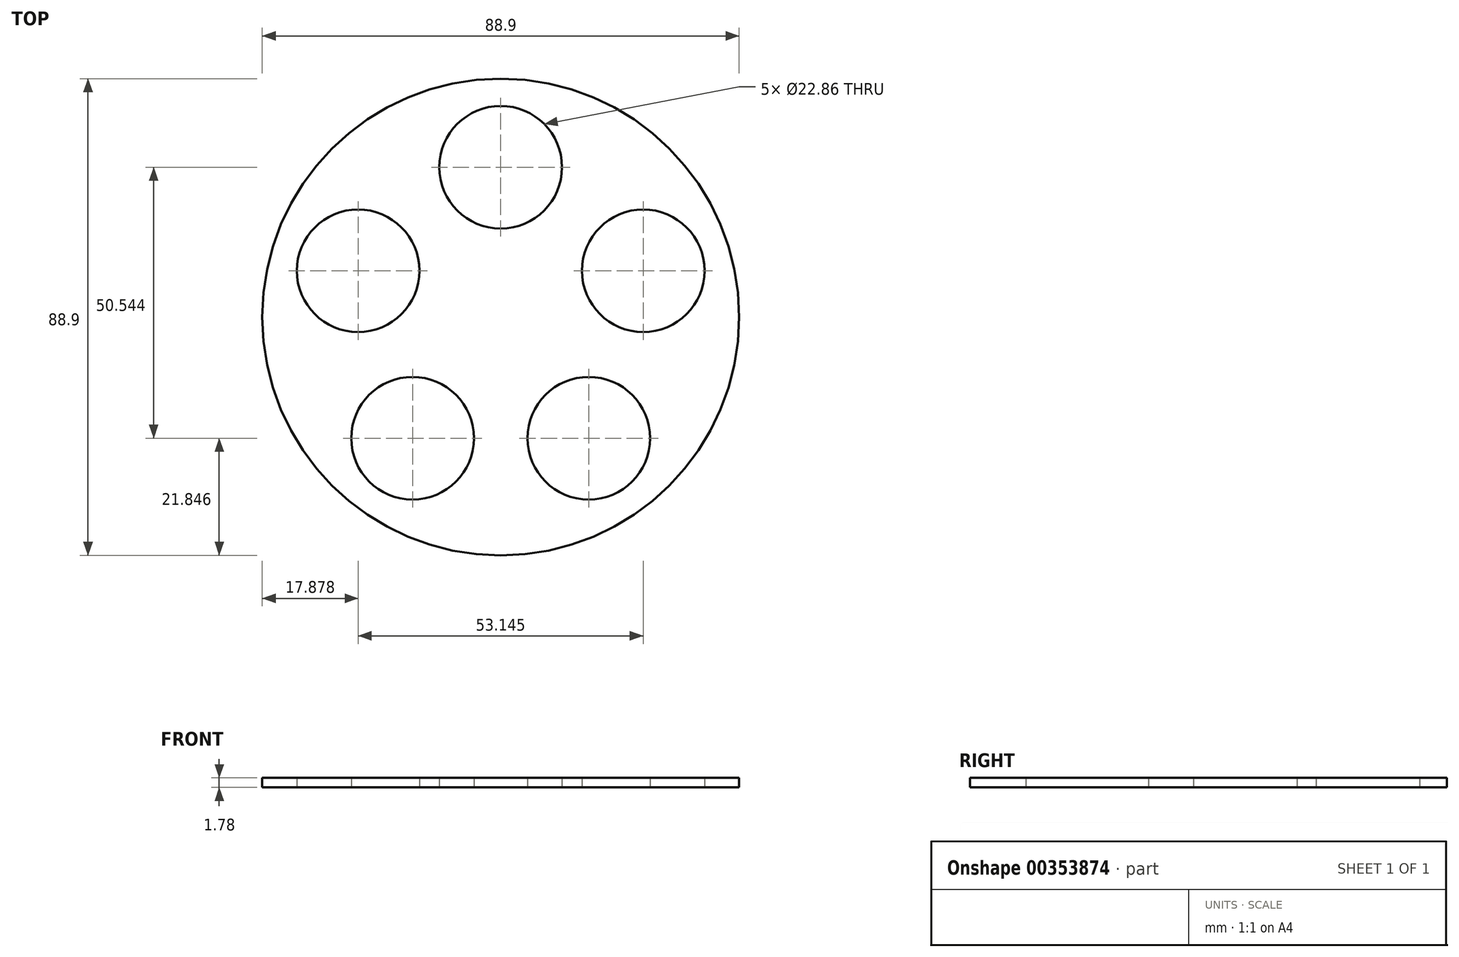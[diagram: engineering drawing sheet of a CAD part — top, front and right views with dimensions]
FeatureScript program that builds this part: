
annotation { "Feature Type Name" : "Feature", "Feature Type Description" : "" }
export const myFeature = defineFeature(function(context is Context, id is Id, definition is map)
    precondition{}
    {
        {
            var Q0;
            Q0=qCreatedBy(makeId("Top.planeOp"),FACE);
            var sketch = newSketch(context, id + "F0", { "sketchPlane" : qUnion([Q0])});
            skCircle(sketch, "E0", {"center": v(0, 27.94) * mm, "radius": 11.43 * mm});
            skCircle(sketch, "E1.1.0", {"center": v(-26.57, 8.63) * mm, "radius": 11.43 * mm});
            skCircle(sketch, "E1.2.0", {"center": v(-16.42, -22.6) * mm, "radius": 11.43 * mm});
            skCircle(sketch, "E1.3.0", {"center": v(16.42, -22.6) * mm, "radius": 11.43 * mm});
            skCircle(sketch, "E1.4.0", {"center": v(26.57, 8.63) * mm, "radius": 11.43 * mm});
            skPoint(sketch, "E1.center", {"position": v(0, 0) * mm});
            skCircle(sketch, "E2", {"center": v(0, 0) * mm, "radius": 44.45 * mm});
            skSolve(sketch);
        }
        {
            var Q0;
            Q0=makeQuery(id+"F0.imprint","IMPRINT",FACE,{"disambiguationData":[TD([[makeQuery(id+"F0.imprint","IMPRINT",EDGE,{"derivedFrom":sQuery(id+"F0.wireOp",EDGE,"E0")}),-1.0]])]});
            extrude(context, id + "F1", {"entities" : qUnion([Q0]), "depth" : 1.78 * mm});
        }
    });
